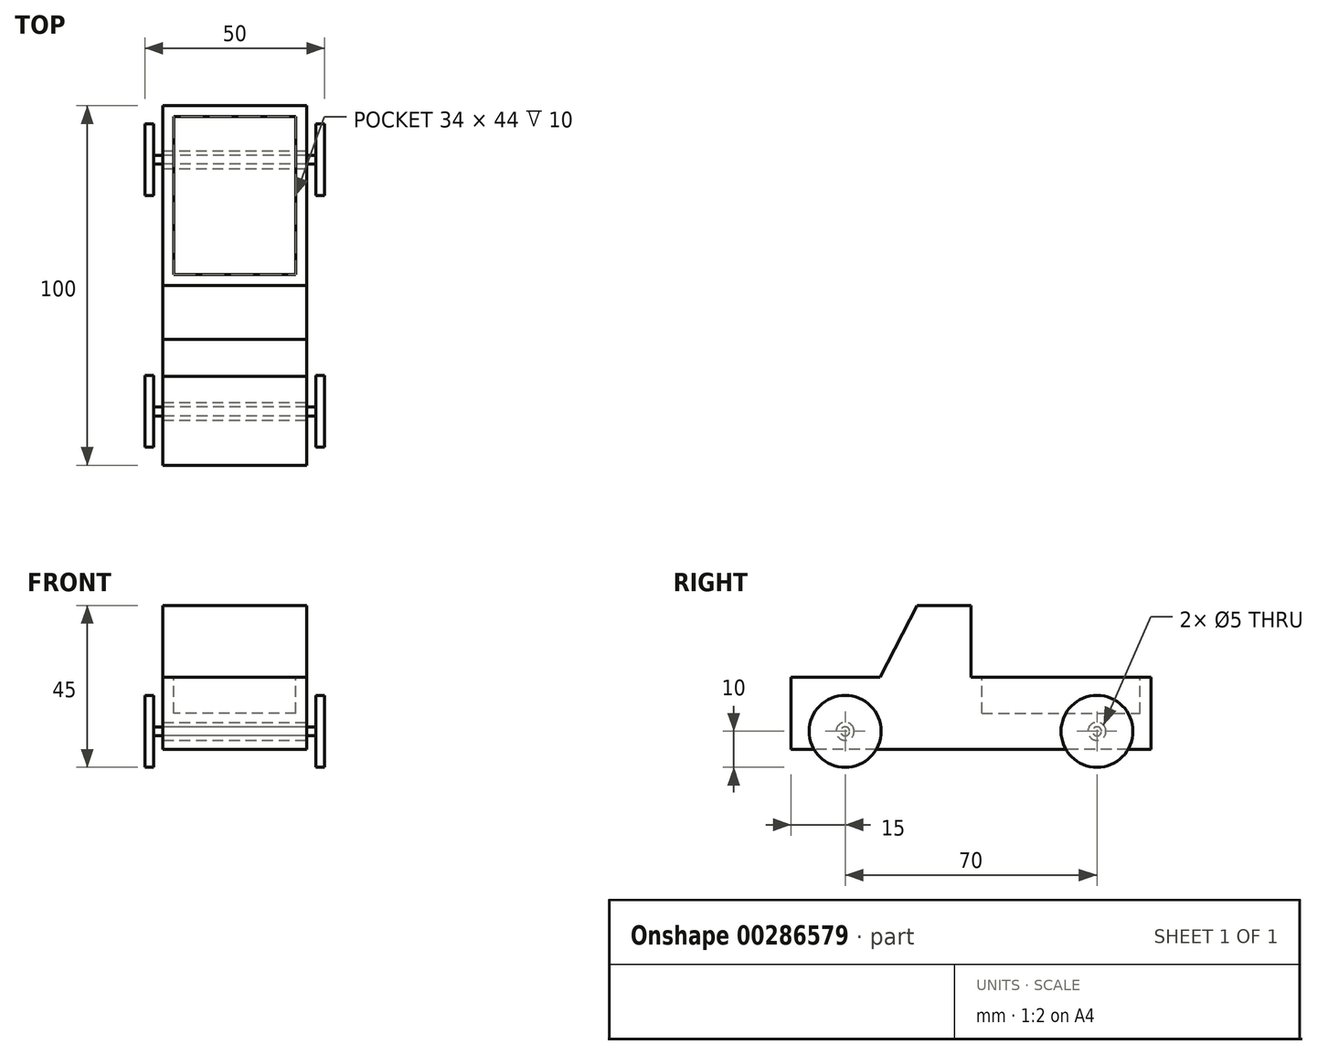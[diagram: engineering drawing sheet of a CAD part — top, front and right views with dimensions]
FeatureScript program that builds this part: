
annotation { "Feature Type Name" : "Feature", "Feature Type Description" : "" }
export const myFeature = defineFeature(function(context is Context, id is Id, definition is map)
    precondition{}
    {
        {
            var Q0;
            Q0=qCreatedBy(makeId("Right.planeOp"),FACE);
            var sketch = newSketch(context, id + "F0", { "sketchPlane" : qUnion([Q0])});
            skLineSegment(sketch, "E0.bottom", {"start": v(50, 10) * mm, "end": v(-50, 10) * mm});
            skLineSegment(sketch, "E0.top", {"start": v(50, -10) * mm, "end": v(-50, -10) * mm});
            skLineSegment(sketch, "E0.left", {"start": v(50, 10) * mm, "end": v(50, -10) * mm});
            skLineSegment(sketch, "E0.right", {"start": v(-50, 10) * mm, "end": v(-50, -10) * mm});
            skPoint(sketch, "E0.middle", {"position": v(0, 0) * mm});
            skLineSegment(sketch, "E1.bottom", {"start": v(0, 10) * mm, "end": v(-15, 10) * mm});
            skLineSegment(sketch, "E1.top", {"start": v(0, 30) * mm, "end": v(-15, 30) * mm});
            skLineSegment(sketch, "E1.left", {"start": v(0, 10) * mm, "end": v(0, 30) * mm});
            skLineSegment(sketch, "E1.right", {"start": v(-15, 10) * mm, "end": v(-15, 30) * mm});
            skLineSegment(sketch, "E2", {"start": v(0, 10) * mm, "end": v(-25.3, 10) * mm});
            skLineSegment(sketch, "E3.bottom", {"start": v(-25.3, 10) * mm, "end": v(-15, 10) * mm});
            skLineSegment(sketch, "E3.top", {"start": v(-25.3, 30) * mm, "end": v(-15, 30) * mm});
            skLineSegment(sketch, "E3.left", {"start": v(-25.3, 10) * mm, "end": v(-25.3, 30) * mm});
            skLineSegment(sketch, "E4", {"start": v(-15, 30) * mm, "end": v(-25.3, 10) * mm});
            skSolve(sketch);
        }
        {
            var Q0;
            Q0 = qSketchRegion(id + "F0", true);
            extrude(context, id + "F1", {"entities" : qUnion([Q0]), "depth" : 40 * mm});
        }
        {
            var Q0;
            Q0 = qSketchRegion(id + "F0", true);
            var Q1;
            Q1=makeQuery(id+"F1.opExtrude","CAP_FACE",FACE,{"disambiguationData":[OSD([sQuery(id+"F0.wireOp",EDGE,"E0.bottom"),sQuery(id+"F0.wireOp",EDGE,"E0.top"),sQuery(id+"F0.wireOp",EDGE,"E0.left"),sQuery(id+"F0.wireOp",EDGE,"E0.right"),sQuery(id+"F0.wireOp",EDGE,"E1.top"),sQuery(id+"F0.wireOp",EDGE,"E1.left"),sQuery(id+"F0.wireOp",EDGE,"E3.top"),sQuery(id+"F0.wireOp",EDGE,"E3.left")])],"isStart":true});
            extrude(context, id + "F2", {"entities" : qUnion([Q0, Q1]), "operationType" : NewBodyOperationType.ADD, "depth" : 25 * mm});
        }
        {
            var Q0;
            Q0=makeQuery(id+"F0.imprint","IMPRINT",FACE,{"disambiguationData":[TD([[makeQuery(id+"F0.imprint","IMPRINT",EDGE,{"derivedFrom":sQuery(id+"F0.wireOp",EDGE,"E3.top")}),-1.0]])]});
            extrude(context, id + "F3", {"entities" : qUnion([Q0]), "operationType" : NewBodyOperationType.REMOVE, "endBound" : BoundingType.THROUGH_ALL, "depth" : 85.7 * mm});
        }
        {
            var Q0;
            Q0=makeQuery(id+"F1.opExtrude","CAP_FACE",FACE,{"disambiguationData":[OSD([sQuery(id+"F0.wireOp",EDGE,"E0.bottom"),sQuery(id+"F0.wireOp",EDGE,"E0.top"),sQuery(id+"F0.wireOp",EDGE,"E0.left"),sQuery(id+"F0.wireOp",EDGE,"E0.right"),sQuery(id+"F0.wireOp",EDGE,"E1.top"),sQuery(id+"F0.wireOp",EDGE,"E1.left"),sQuery(id+"F0.wireOp",EDGE,"E3.top"),sQuery(id+"F0.wireOp",EDGE,"E3.left")])],"isStart":false});
            var sketch = newSketch(context, id + "F4", { "sketchPlane" : qUnion([Q0])});
            skCircle(sketch, "E5", {"center": v(-35, -5) * mm, "radius": 2.5 * mm});
            skCircle(sketch, "E6", {"center": v(35, -5) * mm, "radius": 2.5 * mm});
            skSolve(sketch);
        }
        {
            var Q0;
            Q0 = qSketchRegion(id + "F4", true);
            extrude(context, id + "F5", {"entities" : qUnion([Q0]), "operationType" : NewBodyOperationType.REMOVE, "endBound" : BoundingType.THROUGH_ALL, "oppositeDirection" : true, "depth" : 25 * mm});
        }
        {
            var Q0;
            {var subQ0=sQuery(id+"F0.wireOp",EDGE,"E0.bottom");Q0=makeQuery(id+"F1.opExtrude","SWEPT_FACE",FACE,{"disambiguationData":[OSD([subQ0]),TDD([makeQuery(id+"F0.imprint","IMPRINT",EDGE,{"disambiguationData":[TD([[makeQuery(id+"F0.imprint","INTERSECT",VERTEX,{"derivedFrom":[subQ0,sQuery(id+"F0.wireOp",EDGE,"E0.left")]}),-1.0]])],"derivedFrom":subQ0})])]});}
            var sketch = newSketch(context, id + "F6", { "sketchPlane" : qUnion([Q0])});
            skLineSegment(sketch, "E7.0", {"start": v(37, 47) * mm, "end": v(3, 47) * mm});
            skLineSegment(sketch, "E7.1", {"start": v(37, 3) * mm, "end": v(37, 47) * mm});
            skLineSegment(sketch, "E7.2", {"start": v(3, 3) * mm, "end": v(37, 3) * mm});
            skLineSegment(sketch, "E7.3", {"start": v(3, 47) * mm, "end": v(3, 3) * mm});
            skSolve(sketch);
        }
        {
            var Q0;
            Q0 = qSketchRegion(id + "F6", true);
            extrude(context, id + "F7", {"entities" : qUnion([Q0]), "operationType" : NewBodyOperationType.REMOVE, "oppositeDirection" : true, "depth" : 10 * mm});
        }
        {
            var Q0;
            Q0=qCreatedBy(makeId("Right.planeOp"),FACE);
            var sketch = newSketch(context, id + "F8", { "sketchPlane" : qUnion([Q0])});
            skCircle(sketch, "E8", {"center": v(35, -5) * mm, "radius": 1.25 * mm});
            skCircle(sketch, "E9", {"center": v(-35, -5) * mm, "radius": 1.25 * mm});
            skSolve(sketch);
        }
        {
            var Q0;
            Q0=makeQuery(id+"F8.imprint","IMPRINT",FACE,{"disambiguationData":[TD([[makeQuery(id+"F8.imprint","IMPRINT",EDGE,{"derivedFrom":sQuery(id+"F8.wireOp",EDGE,"E8")}),1.0]])]});
            var Q1;
            Q1=makeQuery(id+"F8.imprint","IMPRINT",FACE,{"disambiguationData":[TD([[makeQuery(id+"F8.imprint","IMPRINT",EDGE,{"derivedFrom":sQuery(id+"F8.wireOp",EDGE,"E9")}),1.0]])]});
            extrude(context, id + "F9", {"entities" : qUnion([Q0, Q1]), "depth" : 42.5 * mm});
        }
        {
            var Q0;
            Q0=makeQuery(id+"F9.opExtrude","CAP_FACE",FACE,{"disambiguationData":[OSD([sQuery(id+"F8.wireOp",EDGE,"E8")])],"isStart":true});
            extrude(context, id + "F10", {"entities" : qUnion([Q0]), "operationType" : NewBodyOperationType.ADD, "depth" : 2.5 * mm});
        }
        {
            var Q0;
            Q0=makeQuery(id+"F9.opExtrude","CAP_FACE",FACE,{"disambiguationData":[OSD([sQuery(id+"F8.wireOp",EDGE,"E9")])],"isStart":true});
            extrude(context, id + "F11", {"entities" : qUnion([Q0]), "operationType" : NewBodyOperationType.ADD, "depth" : 2.5 * mm});
        }
        {
            var Q0;
            Q0=makeQuery(id+"F10.opExtrude","CAP_FACE",FACE,{"disambiguationData":[OSD([sQuery(id+"F8.wireOp",EDGE,"E8")])],"isStart":false});
            var sketch = newSketch(context, id + "F12", { "sketchPlane" : qUnion([Q0])});
            skCircle(sketch, "E10", {"center": v(-35, -5) * mm, "radius": 10 * mm});
            skSolve(sketch);
        }
        {
            var Q0;
            Q0 = qSketchRegion(id + "F12", true);
            extrude(context, id + "F13", {"entities" : qUnion([Q0]), "operationType" : NewBodyOperationType.ADD, "depth" : 2.5 * mm});
        }
        {
            var Q0;
            Q0=makeQuery(id+"F11.opExtrude","CAP_FACE",FACE,{"disambiguationData":[OSD([sQuery(id+"F8.wireOp",EDGE,"E9")])],"isStart":false});
            var sketch = newSketch(context, id + "F14", { "sketchPlane" : qUnion([Q0])});
            skCircle(sketch, "E11", {"center": v(35, -5) * mm, "radius": 10 * mm});
            skSolve(sketch);
        }
        {
            var Q0;
            Q0 = qSketchRegion(id + "F14", true);
            extrude(context, id + "F15", {"entities" : qUnion([Q0]), "operationType" : NewBodyOperationType.ADD, "depth" : 2.5 * mm});
        }
        {
            var Q0;
            Q0=makeQuery(id+"F9.opExtrude","CAP_FACE",FACE,{"disambiguationData":[OSD([sQuery(id+"F8.wireOp",EDGE,"E9")])],"isStart":false});
            var sketch = newSketch(context, id + "F16", { "sketchPlane" : qUnion([Q0])});
            skCircle(sketch, "E12", {"center": v(-35, -5) * mm, "radius": 10 * mm});
            skSolve(sketch);
        }
        {
            var Q0;
            Q0 = qSketchRegion(id + "F16", true);
            extrude(context, id + "F17", {"entities" : qUnion([Q0]), "operationType" : NewBodyOperationType.ADD, "depth" : 2.5 * mm});
        }
        {
            var Q0;
            Q0=makeQuery(id+"F9.opExtrude","CAP_FACE",FACE,{"disambiguationData":[OSD([sQuery(id+"F8.wireOp",EDGE,"E8")])],"isStart":false});
            var sketch = newSketch(context, id + "F18", { "sketchPlane" : qUnion([Q0])});
            skCircle(sketch, "E13", {"center": v(35, -5) * mm, "radius": 10 * mm});
            skSolve(sketch);
        }
        {
            var Q0;
            Q0 = qSketchRegion(id + "F18", true);
            extrude(context, id + "F19", {"entities" : qUnion([Q0]), "operationType" : NewBodyOperationType.ADD, "depth" : 2.5 * mm});
        }
    });
